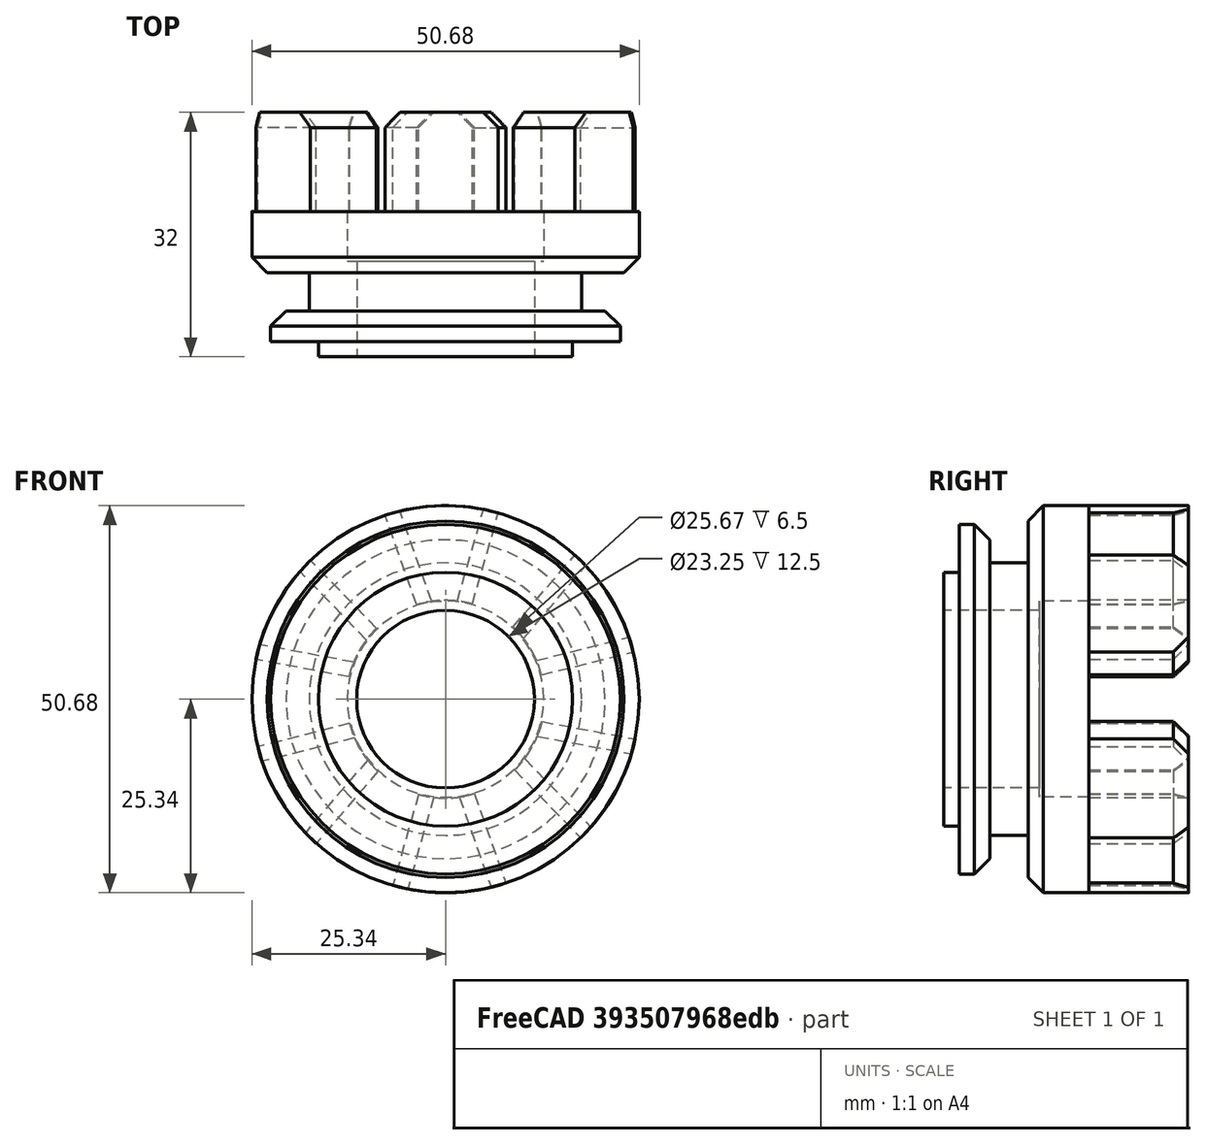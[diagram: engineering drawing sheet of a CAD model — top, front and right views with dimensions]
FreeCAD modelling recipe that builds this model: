
FCSTD DOCUMENT  (FreeCAD 1.0R39319 (Git))
Label: DG rear fixture
License: All rights reserved
LicenseURL: https://en.wikipedia.org/wiki/All_rights_reserved
objects: TechDraw::DrawProjGroupItem×6, TechDraw::DrawViewDimension×6, Sketcher::SketchObject×3, PartDesign::Chamfer×3, PartDesign::Revolution×1, PartDesign::Pad×1, PartDesign::PolarPattern×1, PartDesign::Body×1, TechDraw::DrawSVGTemplate×1, TechDraw::DrawProjGroup×1, TechDraw::DrawPage×1
note: 31 computed .brp shape members not serialized (recipe doc carries the construction recipe); baked Part::Feature solids carry a one-line shape summary decoded from their .brp

FEATURE [Sketcher::SketchObject] Sketch
  ArcFitTolerance = 1e-06
  AttachmentSupport = -> [XY_Plane]
  FullyConstrained = false
  MakeInternals = false
  MapMode = 5
  sketch-geometry (12):
    g0: LineSegment StartX=-11.6235 StartY=80.6195 StartZ=0 EndX=-16.6235 EndY=80.6195 EndZ=0
    g1: LineSegment StartX=-16.6235 StartY=80.6195 StartZ=0 EndX=-16.6235 EndY=82.6195 EndZ=0
    g2: LineSegment StartX=-16.6235 StartY=82.6195 StartZ=0 EndX=-22.8735 EndY=82.6195 EndZ=0
    g3: LineSegment StartX=-22.8735 StartY=82.6195 StartZ=0 EndX=-22.8735 EndY=86.6195 EndZ=0
    g4: LineSegment StartX=-22.8735 StartY=86.6195 StartZ=0 EndX=-17.8374 EndY=86.6195 EndZ=0
    g5: LineSegment StartX=-17.8374 StartY=86.6195 StartZ=0 EndX=-17.8374 EndY=91.6195 EndZ=0
    g6: LineSegment StartX=-17.8374 StartY=91.6195 StartZ=0 EndX=-25.3374 EndY=91.6195 EndZ=0
    g7: LineSegment StartX=-25.3374 StartY=91.6195 StartZ=0 EndX=-25.3374 EndY=99.6195 EndZ=0
    g8: LineSegment StartX=-25.3374 StartY=99.6195 StartZ=0 EndX=-12.8374 EndY=99.6195 EndZ=0
    g9: LineSegment StartX=-12.8374 StartY=99.6195 StartZ=0 EndX=-12.8374 EndY=93.1195 EndZ=0
    g10: LineSegment StartX=-12.8374 StartY=93.1195 StartZ=0 EndX=-11.6235 EndY=93.1195 EndZ=0
    g11: LineSegment StartX=-11.6235 StartY=93.1195 StartZ=0 EndX=-11.6235 EndY=80.6195 EndZ=0
  constraints (33):
    c: Coincident(g0,g1)
    c: Vertical(g1)
    c: Coincident(g1,g2)
    c: Coincident(g2,g3)
    c: Coincident(g3,g4)
    c: Coincident(g4,g5)
    c: Vertical(g5)
    c: Coincident(g5,g6)
    c: Horizontal(g6)
    c: Coincident(g6,g7)
    c: Vertical(g7)
    c: Coincident(g7,g8)
    c: Horizontal(g8)
    c: Horizontal(g0)
    c: Horizontal(g4)
    c: Vertical(g3)
    c: DistanceX(g0,g0) = 5
    c: Horizontal(g2)
    c: DistanceY(g1,g1) = 2
    c: DistanceY(g5,g5) = 5
    c: DistanceY(g3,g3) = 4
    c: DistanceY(g7,g7) = 8
    c: DistanceX(g8,g8) = 12.5
    c: Coincident(g8,g9)
    c: Vertical(g9)
    c: Coincident(g9,g10)
    c: Horizontal(g10)
    c: Coincident(g10,g11)
    c: Vertical(g11)
    c: Coincident(g0,g11)
    c: DistanceX(g6,g6) = 7.5
    c: DistanceY(g9,g9) = 6.5
    c: DistanceX(g2,g2) = 6.25
FEATURE [PartDesign::Revolution] Revolution
  Angle = 360
  Angle2 = 60
  Axis = (0,1,0)
  Base = (0,0,0)
  Profile = -> Sketch
  ReferenceAxis = -> Sketch [V_Axis]
  Refine = true
  Suppressed = false
  Type = 0
FEATURE [Sketcher::SketchObject] Sketch001
  ArcFitTolerance = 1e-06
  AttachmentSupport = -> [Revolution]
  ExternalGeometry = -> [Revolution]
  FullyConstrained = true
  MakeInternals = false
  MapMode = 5
  Placement = pos=(0,99.6195,0) rot=(0,0.707107,0.707107;3.14159rad)
FEATURE [Sketcher::SketchObject] Sketch002
  ArcFitTolerance = 1e-06
  AttachmentSupport = -> [Revolution]
  ExternalGeometry = -> [Revolution]
  FullyConstrained = false
  MakeInternals = false
  MapMode = 5
  Placement = pos=(0,99.6195,0) rot=(0,0.707107,0.707107;3.14159rad)
  sketch-geometry (4):
    g0: LineSegment StartX=3.76804 StartY=12.3822 StartZ=0 EndX=7.894 EndY=24.0763 EndZ=0
    g1: LineSegment StartX=-3.51886 StartY=12.455 StartZ=0 EndX=-6.90332 EndY=24.3789 EndZ=0
    g2: ArcOfCircle CenterX=0.00109817 CenterY=0.0537125 CenterZ=0 NormalX=0 NormalY=0 NormalZ=1 AngleXU=0 Radius=25.2861 StartAngle=1.25335 EndAngle=1.84736
    g3: ArcOfCircle CenterX=0.00109817 CenterY=0.0537125 CenterZ=0 NormalX=0 NormalY=0 NormalZ=1 AngleXU=0 Radius=12.8912 StartAngle=1.27426 EndAngle=1.84736
  constraints (9):
    c: PointOnObject(g1,g-3)
    c: PointOnObject(g0,g-3)
    c: Angle(g0,g1) = 0.615752
    c: Perpendicular(g1,g2) = 1.5708
    c: Coincident(g3,g2)
    c: Tangent(g3,g-4)
    c: Coincident(g1,g3)
    c: Coincident(g0,g3)
    c: Coincident(g2,g0)
FEATURE [PartDesign::Pad] Pad
  BaseFeature = -> Revolution
  Direction = (0,1,-2e-16)
  Length = 13
  Length2 = 10
  Profile = -> Sketch002
  ReferenceAxis = -> Sketch002 [N_Axis]
  Refine = true
  Suppressed = false
  Type = 0
FEATURE [PartDesign::Chamfer] Chamfer
  Angle = 45
  Base = -> Pad [Edge28,Edge24]
  BaseFeature = -> Pad
  ChamferType = 0
  FlipDirection = false
  Refine = true
  Size = 2
  Size2 = 1
  SupportTransform = false
  Suppressed = false
  UseAllEdges = false
FEATURE [PartDesign::PolarPattern] PolarPattern
  Angle = 360
  Axis = -> Sketch002 [N_Axis]
  BaseFeature = -> Chamfer
  Mode = 0
  Occurrences = 6
  Offset = 120
  Originals = -> [Pad]
  Refine = true
  Suppressed = false
  TransformMode = 0
FEATURE [PartDesign::Chamfer] Chamfer001
  Angle = 45
  Base = -> PolarPattern [Edge80,Edge84,Edge77,Edge73,Edge70,Edge66,Edge63,Edge59,Edge56,Edge52]
  BaseFeature = -> PolarPattern
  ChamferType = 0
  FlipDirection = false
  Refine = true
  Size = 2
  Size2 = 1
  SupportTransform = false
  Suppressed = false
  UseAllEdges = false
FEATURE [PartDesign::Chamfer] Chamfer002
  Angle = 45
  Base = -> Chamfer001 [Edge51,Edge133]
  BaseFeature = -> Chamfer001
  ChamferType = 0
  FlipDirection = false
  Refine = true
  Size = 2
  Size2 = 1
  SupportTransform = false
  Suppressed = false
  UseAllEdges = false
FEATURE [PartDesign::Body] Body
  AllowCompound = false
  Group = -> [Sketch,Revolution,Sketch001,Sketch002,Pad,Chamfer,PolarPattern,Chamfer001,Chamfer002]
  Origin = -> Origin
  Tip = -> Chamfer002
FEATURE [TechDraw::DrawSVGTemplate] Template
  EditableTexts = AuthorName=Krushna Manwatkar; CheckDate=CHECK DATE; CreationDate=06-01-2026; DrawingNumber=NUMBER; FC-Title=DG rear fixture; SheetNumber=1 / 1; Subtitle=SUBTITLE; SupervisorName=SUPERVISOR NAME; Weight=WEIGHT; scale=1 : 1
  Height = 297
  Orientation = 1
  Template = C:/Program Files/FreeCAD 1.0/data/Mod/TechDraw/Templates/A3_Landscape_TD.svg
  Width = 420
FEATURE [TechDraw::DrawProjGroupItem] View  label="Front"
  CoarseView = false
  Direction = (0,-1,0)
  Focus = 100
  HardHidden = false
  IsoCount = 0
  IsoHidden = false
  IsoVisible = false
  LockPosition = true
  Perspective = false
  Rotation = 0
  RotationVector = (1,0,0)
  ScaleType = 2
  ScrubCount = 1
  SeamHidden = false
  SeamVisible = false
  SmoothHidden = false
  SmoothVisible = true
  Source = -> [Body]
  Type = 0
  X = 0
  XDirection = (1,0,0)
  Y = 0
FEATURE [TechDraw::DrawProjGroupItem] ProjItem  label="Bottom"
  CoarseView = false
  Direction = (0,0,-1)
  Focus = 100
  HardHidden = false
  IsoCount = 0
  IsoHidden = false
  IsoVisible = false
  LockPosition = false
  Perspective = false
  Rotation = 0
  RotationVector = (1,0,0)
  ScaleType = 0
  ScrubCount = 1
  SeamHidden = false
  SeamVisible = false
  SmoothHidden = false
  SmoothVisible = true
  Source = -> [Body]
  Type = 5
  X = 0
  XDirection = (1,0,0)
  Y = -68.0602
FEATURE [TechDraw::DrawProjGroupItem] ProjItem001  label="FrontBottomRight"
  CoarseView = false
  Direction = (0.57735,-0.57735,-0.57735)
  Focus = 100
  HardHidden = false
  IsoCount = 0
  IsoHidden = false
  IsoVisible = false
  LockPosition = false
  Perspective = false
  Rotation = 0
  RotationVector = (1,0,0)
  ScaleType = 0
  ScrubCount = 1
  SeamHidden = false
  SeamVisible = false
  SmoothHidden = false
  SmoothVisible = true
  Source = -> [Body]
  Type = 9
  X = 67.626
  XDirection = (0.707107,0.707107,0)
  Y = -68.0602
FEATURE [TechDraw::DrawProjGroupItem] ProjItem002  label="Right"
  CoarseView = false
  Direction = (1,-1e-16,0)
  Focus = 100
  HardHidden = false
  IsoCount = 0
  IsoHidden = false
  IsoVisible = false
  LockPosition = false
  Perspective = false
  Rotation = 0
  RotationVector = (1,0,0)
  ScaleType = 0
  ScrubCount = 1
  SeamHidden = false
  SeamVisible = false
  SmoothHidden = false
  SmoothVisible = true
  Source = -> [Body]
  Type = 2
  X = 70.1482
  XDirection = (1e-16,1,0)
  Y = 0
FEATURE [TechDraw::DrawProjGroupItem] ProjItem003  label="Rear"
  CoarseView = false
  Direction = (0,1,0)
  Focus = 100
  HardHidden = false
  IsoCount = 0
  IsoHidden = false
  IsoVisible = false
  LockPosition = false
  Perspective = false
  Rotation = 0
  RotationVector = (1,0,0)
  ScaleType = 0
  ScrubCount = 1
  SeamHidden = false
  SeamVisible = false
  SmoothHidden = false
  SmoothVisible = true
  Source = -> [Body]
  Type = 3
  X = 135.252
  XDirection = (-1,0,0)
  Y = 0
FEATURE [TechDraw::DrawProjGroupItem] ProjItem004  label="FrontTopRight"
  CoarseView = false
  Direction = (0.57735,-0.57735,0.57735)
  Focus = 100
  HardHidden = false
  IsoCount = 0
  IsoHidden = false
  IsoVisible = false
  LockPosition = false
  Perspective = false
  Rotation = 0
  RotationVector = (1,0,0)
  ScaleType = 0
  ScrubCount = 1
  SeamHidden = false
  SeamVisible = false
  SmoothHidden = false
  SmoothVisible = true
  Source = -> [Body]
  Type = 7
  X = 67.626
  XDirection = (0.707107,0.707107,0)
  Y = 68.1753
FEATURE [TechDraw::DrawProjGroup] ProjGroup
  Anchor = -> View
  AutoDistribute = true
  LockPosition = false
  ProjectionType = 1
  Rotation = 0
  ScaleType = 0
  Source = -> [Body]
  Views = -> [View,ProjItem,ProjItem001,ProjItem002,ProjItem003,ProjItem004]
  X = 75.7694
  Y = 162.557
  spacingX = 15
  spacingY = 15
FEATURE [TechDraw::DrawViewDimension] Dimension
  AngleOverride = false
  Arbitrary = false
  ArbitraryTolerances = false
  BoxCorners = (2) [(-25.3374,-25.3398,0),(25.3374,25.3398,0)]
  EqualTolerance = true
  ExtensionAngle = 0
  FormatSpec = ⌀%.2w
  FormatSpecOverTolerance = %+.2w
  FormatSpecUnderTolerance = %+.2w
  Inverted = false
  LineAngle = 0
  LockPosition = false
  MeasureType = 1
  OverTolerance = 0
  References2D = -> [View]
  Rotation = 0
  ScaleType = 0
  TheoreticalExact = false
  Type = 5
  UnderTolerance = 0
  X = 10.0981
  Y = 68.3882
FEATURE [TechDraw::DrawViewDimension] Dimension001
  AngleOverride = false
  Arbitrary = false
  ArbitraryTolerances = false
  BoxCorners = (2) [(-25.3374,-25.3398,0),(25.3374,25.3398,0)]
  EqualTolerance = true
  ExtensionAngle = 0
  FormatSpec = ⌀%.2w
  FormatSpecOverTolerance = %+.2w
  FormatSpecUnderTolerance = %+.2w
  Inverted = false
  LineAngle = 0
  LockPosition = false
  MeasureType = 1
  OverTolerance = 0
  References2D = -> [View]
  Rotation = 0
  ScaleType = 0
  TheoreticalExact = false
  Type = 5
  UnderTolerance = 0
  X = 46.5914
  Y = 15.0634
FEATURE [TechDraw::DrawViewDimension] Dimension002
  AngleOverride = false
  Arbitrary = false
  ArbitraryTolerances = false
  BoxCorners = (2) [(-25.3374,-25.3398,0),(25.3374,25.3398,0)]
  EqualTolerance = true
  ExtensionAngle = 0
  FormatSpec = ⌀%.2w
  FormatSpecOverTolerance = %+.2w
  FormatSpecUnderTolerance = %+.2w
  Inverted = false
  LineAngle = 0
  LockPosition = false
  MeasureType = 1
  OverTolerance = 0
  References2D = -> [View]
  Rotation = 0
  ScaleType = 0
  TheoreticalExact = false
  Type = 5
  UnderTolerance = 0
  X = -19.3925
  Y = 45.1141
FEATURE [TechDraw::DrawViewDimension] Dimension003
  AngleOverride = false
  Arbitrary = false
  ArbitraryTolerances = false
  BoxCorners = (2) [(-16,-25.3398,-1e-07),(16,25.3398,1e-07)]
  EqualTolerance = true
  ExtensionAngle = 0
  FormatSpec = %.2w
  FormatSpecOverTolerance = %+.2w
  FormatSpecUnderTolerance = %+.2w
  Inverted = false
  LineAngle = 0
  LockPosition = false
  MeasureType = 1
  OverTolerance = 0
  References2D = -> [ProjItem002]
  Rotation = 0
  ScaleType = 0
  TheoreticalExact = false
  Type = 2
  UnderTolerance = 0
  X = 123.643
  Y = 6.60777
FEATURE [TechDraw::DrawViewDimension] Dimension004
  AngleOverride = false
  Arbitrary = false
  ArbitraryTolerances = false
  BoxCorners = (2) [(-25.3374,-25.3398,-1e-07),(25.3374,25.3398,1e-07)]
  EqualTolerance = true
  ExtensionAngle = 0
  FormatSpec = R%.2w
  FormatSpecOverTolerance = %+.2w
  FormatSpecUnderTolerance = %+.2w
  Inverted = false
  LineAngle = 0
  LockPosition = false
  MeasureType = 1
  OverTolerance = 0
  References2D = -> [ProjItem003]
  Rotation = 0
  ScaleType = 0
  TheoreticalExact = false
  Type = 4
  UnderTolerance = 0
  X = 33.826
  Y = 48.694
FEATURE [TechDraw::DrawViewDimension] Dimension005
  AngleOverride = false
  Arbitrary = false
  ArbitraryTolerances = false
  BoxCorners = (2) [(-16,-25.3398,-1e-07),(16,25.3398,1e-07)]
  EqualTolerance = true
  ExtensionAngle = 0
  FormatSpec = %.2w
  FormatSpecOverTolerance = %+.2w
  FormatSpecUnderTolerance = %+.2w
  Inverted = false
  LineAngle = 0
  LockPosition = false
  MeasureType = 1
  OverTolerance = 0
  References2D = -> [ProjItem002]
  Rotation = 0
  ScaleType = 0
  TheoreticalExact = false
  Type = 0
  UnderTolerance = 0
  X = 152.295
  Y = -10.7467
FEATURE [TechDraw::DrawPage] Page
  KeepUpdated = true
  NextBalloonIndex = 1
  ProjectionType = 0
  Template = -> Template
  Views = -> [ProjGroup,Dimension,Dimension001,Dimension002,Dimension003,Dimension004,Dimension005]
